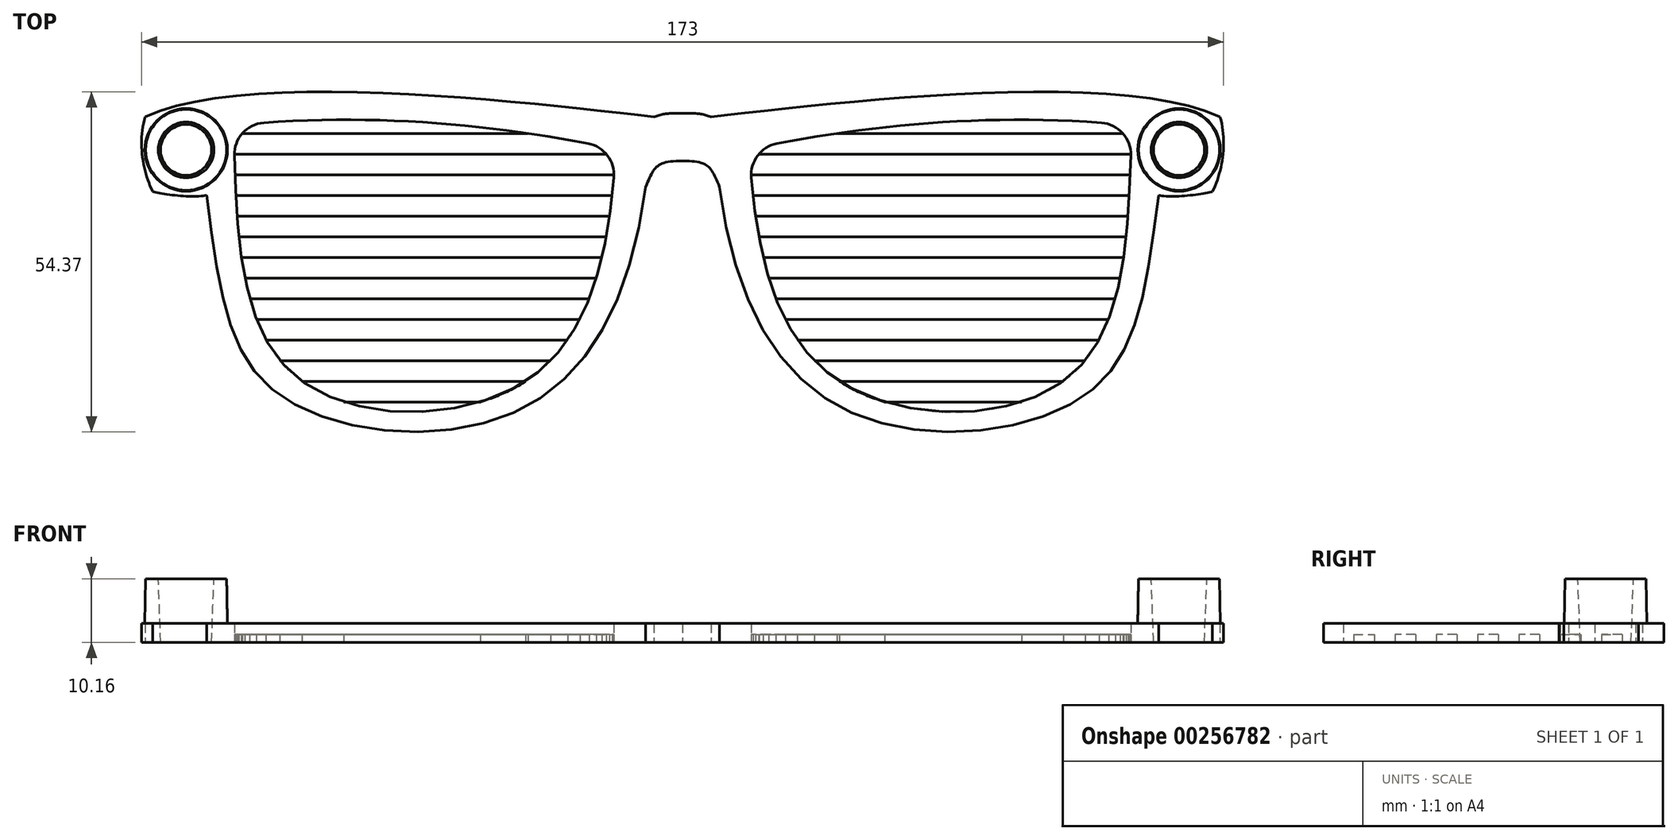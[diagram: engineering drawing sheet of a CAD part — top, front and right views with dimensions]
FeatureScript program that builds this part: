
annotation { "Feature Type Name" : "Feature", "Feature Type Description" : "" }
export const myFeature = defineFeature(function(context is Context, id is Id, definition is map)
    precondition{}
    {
        {
            var Q0;
            Q0=qCreatedBy(makeId("Top.planeOp"),FACE);
            var sketch = newSketch(context, id + "F0", { "sketchPlane" : qUnion([Q0])});
            skFitSpline(sketch, "E0", {"points": [v(0, -1.25) * mm, v(-4.57, -1.84) * mm], "startDerivative": vector(-4.29, -0.03) * mm, "endDerivative": vector(-4.84, -1.9) * mm});
            skFitSpline(sketch, "E1", {"points": [v(-4.57, -1.84) * mm, v(-85.93, -1.84) * mm], "startDerivative": vector(-55.54, 6.07) * mm, "endDerivative": vector(-50.97, -23.71) * mm});
            skFitSpline(sketch, "E2", {"points": [v(-76.11, -14.35) * mm, v(-64.79, -46.04) * mm, v(-27.62, -49.4) * mm, v(-5.92, -13.06) * mm], "startDerivative": vector(19.74, -143.66) * mm, "endDerivative": vector(20.37, 155.62) * mm});
            skFitSpline(sketch, "E3", {"points": [v(-5.92, -13.06) * mm, v(0, -8.87) * mm], "startDerivative": vector(4.13, 9.55) * mm, "endDerivative": vector(13.05, 0) * mm});
            skLineSegment(sketch, "E4", {"start": v(0, -1.25) * mm, "end": v(0, -8.87) * mm});
            skFitSpline(sketch, "E5", {"points": [v(-85.93, -1.84) * mm, v(-84.72, -13.81) * mm], "startDerivative": vector(-3.44, -12.2) * mm, "endDerivative": vector(4.98, -10.41) * mm});
            skFitSpline(sketch, "E6", {"points": [v(-84.72, -13.81) * mm, v(-76.11, -14.35) * mm], "startDerivative": vector(4.96, -1.42) * mm, "endDerivative": vector(5.45, 1.47) * mm});
            skCircle(sketch, "E7", {"center": v(-79.38, -7.12) * mm, "radius": 4.25 * mm});
            skFitSpline(sketch, "E8", {"points": [v(-10.67, -7.02) * mm, v(-24.61, -43.79) * mm, v(-62.05, -43.18) * mm, v(-71.83, -3.21) * mm], "startDerivative": vector(-7.94, -134.67) * mm, "endDerivative": vector(-5.24, 133.94) * mm});
            skFitSpline(sketch, "E9", {"points": [v(-71.83, -3.21) * mm, v(-10.67, -7.02) * mm], "startDerivative": vector(63.48, 6.5) * mm, "endDerivative": vector(56.84, -12.23) * mm});
            skSolve(sketch);
        }
        {
            var Q0;
            Q0=makeQuery(id+"F0.imprint","IMPRINT",FACE,{"disambiguationData":[TD([[makeQuery(id+"F0.imprint","IMPRINT",EDGE,{"derivedFrom":sQuery(id+"F0.wireOp",EDGE,"E0")}),1.0]])]});
            extrude(context, id + "F1", {"entities" : qUnion([Q0]), "depth" : 3.05 * mm});
        }
        {
            var Q0;
            {var subQ0=sQuery(id+"F0.wireOp",EDGE,"E9");var subQ1=sQuery(id+"F0.wireOp",EDGE,"E8");Q0=makeQuery(id+"F1.opExtrude","SWEPT_EDGE",EDGE,{"disambiguationData":[OSD([subQ1,subQ0]),TDD([makeQuery(id+"F0.imprint","INTERSECT",VERTEX,{"disambiguationData":[OD(1.0)],"derivedFrom":[subQ1,subQ0]})])]});}
            var Q1;
            {var subQ0=sQuery(id+"F0.wireOp",EDGE,"E9");var subQ1=sQuery(id+"F0.wireOp",EDGE,"E8");Q1=makeQuery(id+"F1.opExtrude","SWEPT_EDGE",EDGE,{"disambiguationData":[OSD([subQ1,subQ0]),TDD([makeQuery(id+"F0.imprint","INTERSECT",VERTEX,{"disambiguationData":[OD(0.0)],"derivedFrom":[subQ1,subQ0]})])]});}
            fillet(context, id + "F2", {"entities" : qUnion([Q0, Q1]), "radius" : 5.08 * mm, "tangentPropagation" : true, "allowEdgeOverflow" : false});
        }
        {
            var Q0;
            Q0=qCreatedBy(makeId("Top.planeOp"),FACE);
            var sketch = newSketch(context, id + "F3", { "sketchPlane" : qUnion([Q0])});
            skLineSegment(sketch, "E10.bottom", {"start": v(-72.86, -4.48) * mm, "end": v(-7.58, -4.48) * mm});
            skLineSegment(sketch, "E10.top", {"start": v(-72.86, -7.78) * mm, "end": v(-7.58, -7.78) * mm});
            skLineSegment(sketch, "E10.left", {"start": v(-72.86, -4.48) * mm, "end": v(-72.86, -7.78) * mm});
            skLineSegment(sketch, "E10.right", {"start": v(-7.58, -4.48) * mm, "end": v(-7.58, -7.78) * mm});
            skLineSegment(sketch, "E11.bottom", {"start": v(-73.3, -11.08) * mm, "end": v(-9.13, -11.08) * mm});
            skLineSegment(sketch, "E11.top", {"start": v(-73.3, -14.39) * mm, "end": v(-9.13, -14.39) * mm});
            skLineSegment(sketch, "E11.left", {"start": v(-73.3, -11.08) * mm, "end": v(-73.3, -14.39) * mm});
            skLineSegment(sketch, "E11.right", {"start": v(-9.13, -11.08) * mm, "end": v(-9.13, -14.39) * mm});
            skLineSegment(sketch, "E12.bottom", {"start": v(-10.38, -17.69) * mm, "end": v(-73, -17.69) * mm});
            skLineSegment(sketch, "E12.top", {"start": v(-10.38, -21) * mm, "end": v(-73, -21) * mm});
            skLineSegment(sketch, "E12.left", {"start": v(-10.38, -17.69) * mm, "end": v(-10.38, -21) * mm});
            skLineSegment(sketch, "E12.right", {"start": v(-73, -17.69) * mm, "end": v(-73, -21) * mm});
            skLineSegment(sketch, "E13.bottom", {"start": v(-11.59, -24.3) * mm, "end": v(-71.88, -24.3) * mm});
            skLineSegment(sketch, "E13.top", {"start": v(-11.59, -27.6) * mm, "end": v(-71.88, -27.6) * mm});
            skLineSegment(sketch, "E13.left", {"start": v(-11.59, -24.3) * mm, "end": v(-11.59, -27.6) * mm});
            skLineSegment(sketch, "E13.right", {"start": v(-71.88, -24.3) * mm, "end": v(-71.88, -27.6) * mm});
            skLineSegment(sketch, "E14.bottom", {"start": v(-13.43, -30.9) * mm, "end": v(-70.24, -30.9) * mm});
            skLineSegment(sketch, "E14.top", {"start": v(-13.43, -34.2) * mm, "end": v(-70.24, -34.2) * mm});
            skLineSegment(sketch, "E14.left", {"start": v(-13.43, -30.9) * mm, "end": v(-13.43, -34.2) * mm});
            skLineSegment(sketch, "E14.right", {"start": v(-70.24, -30.9) * mm, "end": v(-70.24, -34.2) * mm});
            skLineSegment(sketch, "E15.bottom", {"start": v(-17.26, -37.5) * mm, "end": v(-68.12, -37.5) * mm});
            skLineSegment(sketch, "E15.top", {"start": v(-17.26, -40.8) * mm, "end": v(-68.12, -40.8) * mm});
            skLineSegment(sketch, "E15.left", {"start": v(-17.26, -37.5) * mm, "end": v(-17.26, -40.8) * mm});
            skLineSegment(sketch, "E15.right", {"start": v(-68.12, -37.5) * mm, "end": v(-68.12, -40.8) * mm});
            skLineSegment(sketch, "E16.bottom", {"start": v(-61.73, -44.1) * mm, "end": v(-24.35, -44.1) * mm});
            skLineSegment(sketch, "E16.top", {"start": v(-61.73, -47.4) * mm, "end": v(-24.35, -47.4) * mm});
            skLineSegment(sketch, "E16.left", {"start": v(-61.73, -44.1) * mm, "end": v(-61.73, -47.4) * mm});
            skLineSegment(sketch, "E16.right", {"start": v(-24.35, -44.1) * mm, "end": v(-24.35, -47.4) * mm});
            skSolve(sketch);
        }
        {
            var Q0;
            Q0=qSketchRegion(id+"F3",true);
            extrude(context, id + "F4", {"entities" : qUnion([Q0]), "operationType" : NewBodyOperationType.ADD, "depth" : 1.27 * mm});
        }
        {
            var Q0;
            Q0=qCreatedBy(makeId("Top.planeOp"),FACE);
            var sketch = newSketch(context, id + "F5", { "sketchPlane" : qUnion([Q0])});
            skPoint(sketch, "E17", {"position": v(-79.38, -7.12) * mm});
            skSolve(sketch);
        }
        {
            var Q0;
            Q0=qCreatedBy(makeId("Front.planeOp"),FACE);
            var Q1;
            Q1=sQuery(id+"F5.wireOp",VERTEX,"E17");
            cPlane(context, id + "F6", {"entities" : qUnion([Q0, Q1]), "cplaneType" : CPlaneType.PLANE_POINT, "offset" : 152.4 * mm, "width" : 152.4 * mm, "height" : 152.4 * mm});
        }
        {
            var Q0;
            Q0=qCreatedBy(id+"F6.planeOp",FACE);
            var sketch = newSketch(context, id + "F7", { "sketchPlane" : qUnion([Q0])});
            skLineSegment(sketch, "E18", {"start": v(-79.38, 11.21) * mm, "end": v(-79.38, -6.37) * mm, "construction": true});
            skSolve(sketch);
        }
        {
            var Q0;
            Q0=qCreatedBy(id+"F6.planeOp",FACE);
            var sketch = newSketch(context, id + "F8", { "sketchPlane" : qUnion([Q0])});
            skLineSegment(sketch, "E19", {"start": v(-85.85, 10.16) * mm, "end": v(-83.82, 10.16) * mm});
            skLineSegment(sketch, "E20", {"start": v(-83.82, 10.16) * mm, "end": v(-83.44, 0) * mm});
            skLineSegment(sketch, "E21", {"start": v(-83.44, 0) * mm, "end": v(-86.04, 0) * mm});
            skLineSegment(sketch, "E22", {"start": v(-86.04, 0) * mm, "end": v(-85.85, 10.16) * mm});
            skSolve(sketch);
        }
        {
            var Q0;
            Q0=makeQuery(id+"F8.imprint","IMPRINT",FACE,{"disambiguationData":[TD([[makeQuery(id+"F8.imprint","IMPRINT",EDGE,{"derivedFrom":sQuery(id+"F8.wireOp",EDGE,"E19")}),-1.0]])]});
            var Q1;
            Q1=sQuery(id+"F7.wireOp",EDGE,"E18");
            revolve(context, id + "F9", {"operationType" : NewBodyOperationType.ADD, "entities" : qUnion([Q0]), "axis" : qUnion([Q1]), "revolveType" : RevolveType.FULL});
        }
        {
            var Q0;
            Q0=makeQuery(id+"F1.opExtrude","SWEPT_BODY",BODY,{"disambiguationData":[OSD([sQuery(id+"F0.wireOp",EDGE,"E0"),sQuery(id+"F0.wireOp",EDGE,"E1"),sQuery(id+"F0.wireOp",EDGE,"49ca96db-4137-404c-acfc-dd4352609506"),sQuery(id+"F0.wireOp",EDGE,"E2"),sQuery(id+"F0.wireOp",EDGE,"E3"),sQuery(id+"F0.wireOp",EDGE,"E4")])]});
            var Q1;
            Q1=qCreatedBy(makeId("Right.planeOp"),FACE);
            mirror(context, id + "F10", {"operationType" : NewBodyOperationType.ADD, "entities" : qUnion([Q0]), "mirrorPlane" : qUnion([Q1])});
        }
    });
